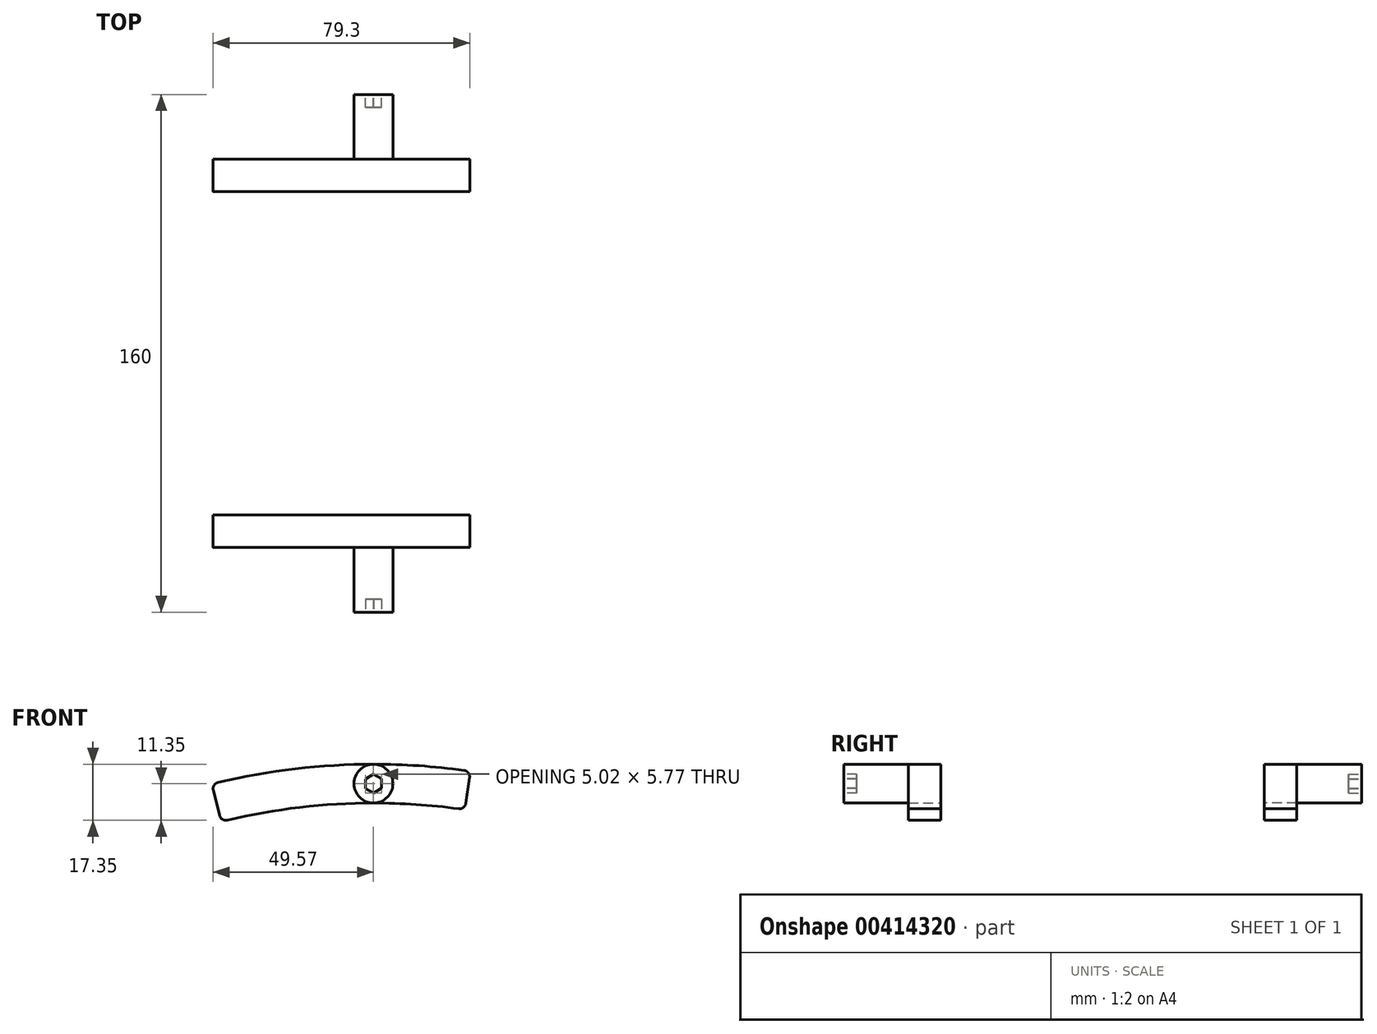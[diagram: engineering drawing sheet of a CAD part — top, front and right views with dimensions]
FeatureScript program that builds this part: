
annotation { "Feature Type Name" : "Feature", "Feature Type Description" : "" }
export const myFeature = defineFeature(function(context is Context, id is Id, definition is map)
    precondition{}
    {
        {
            var Q0;
            Q0=qCreatedBy(makeId("Front.planeOp"),FACE);
            var sketch = newSketch(context, id + "F0", { "sketchPlane" : qUnion([Q0])});
            skLineSegment(sketch, "E0", {"start": v(0, 0) * mm, "end": v(0, 276.46) * mm});
            skCircle(sketch, "E1", {"center": v(0, 0) * mm, "radius": 201.5 * mm, "construction": true});
            skCircle(sketch, "E2", {"center": v(0, 201.5) * mm, "radius": 3 * mm});
            skCircle(sketch, "E3", {"center": v(0, 201.5) * mm, "radius": 6 * mm});
            skArc(sketch, "E4", {"start": v(28, 205.6) * mm, "mid": v(-10.2, 207.25) * mm, "end": v(-48.04, 201.86) * mm});
            skArc(sketch, "E5", {"start": v(26.3, 193.72) * mm, "mid": v(-9.6, 195.26) * mm, "end": v(-45.18, 190.2) * mm});
            skLineSegment(sketch, "E6", {"start": v(28.55, 195.41) * mm, "end": v(29.7, 203.33) * mm});
            skLineSegment(sketch, "E7", {"start": v(-47.59, 191.67) * mm, "end": v(-49.52, 199.44) * mm});
            skPoint(sketch, "E8.visualSharp", {"position": v(30, 205.32) * mm});
            skArc(sketch, "E8.filletArc", {"start": v(29.7, 203.33) * mm, "mid": v(29.33, 204.82) * mm, "end": v(28, 205.6) * mm});
            skPoint(sketch, "E9.visualSharp", {"position": v(28.27, 193.45) * mm});
            skArc(sketch, "E9.filletArc", {"start": v(26.3, 193.72) * mm, "mid": v(27.78, 194.1) * mm, "end": v(28.55, 195.41) * mm});
            skPoint(sketch, "E10.visualSharp", {"position": v(-47.1, 189.74) * mm});
            skArc(sketch, "E10.filletArc", {"start": v(-47.59, 191.67) * mm, "mid": v(-46.69, 190.44) * mm, "end": v(-45.18, 190.2) * mm});
            skPoint(sketch, "E11.visualSharp", {"position": v(-50, 201.39) * mm});
            skArc(sketch, "E11.filletArc", {"start": v(-48.04, 201.86) * mm, "mid": v(-49.28, 200.96) * mm, "end": v(-49.52, 199.44) * mm});
            skSolve(sketch);
        }
        {
            var Q0;
            Q0=makeQuery(id+"F0.imprint","IMPRINT",FACE,{"disambiguationData":[TD([[makeQuery(id+"F0.imprint","IMPRINT",EDGE,{"derivedFrom":sQuery(id+"F0.wireOp",EDGE,"E7")}),-1.0]])]});
            var Q1;
            {var subQ0=sQuery(id+"F0.wireOp",EDGE,"E2");var subQ1=sQuery(id+"F0.wireOp",EDGE,"E0");var subQ2=makeQuery(id+"F0.imprint","INTERSECT",VERTEX,{"disambiguationData":[OD(0.0)],"derivedFrom":[subQ1,subQ0]});Q1=makeQuery(id+"F0.imprint","IMPRINT",FACE,{"disambiguationData":[TD([[makeQuery(id+"F0.imprint","IMPRINT",EDGE,{"disambiguationData":[TD([[subQ2,1.0]])],"derivedFrom":subQ0}),-1.0]])]});}
            var Q2;
            {var subQ0=sQuery(id+"F0.wireOp",EDGE,"E2");var subQ1=sQuery(id+"F0.wireOp",EDGE,"E0");var subQ2=makeQuery(id+"F0.imprint","INTERSECT",VERTEX,{"disambiguationData":[OD(0.0)],"derivedFrom":[subQ1,subQ0]});Q2=makeQuery(id+"F0.imprint","IMPRINT",FACE,{"disambiguationData":[TD([[makeQuery(id+"F0.imprint","IMPRINT",EDGE,{"disambiguationData":[TD([[subQ2,-1.0]])],"derivedFrom":subQ1}),-1.0]])]});}
            var Q3;
            {var subQ0=sQuery(id+"F0.wireOp",EDGE,"E2");var subQ1=sQuery(id+"F0.wireOp",EDGE,"E0");var subQ2=makeQuery(id+"F0.imprint","INTERSECT",VERTEX,{"disambiguationData":[OD(0.0)],"derivedFrom":[subQ1,subQ0]});Q3=makeQuery(id+"F0.imprint","IMPRINT",FACE,{"disambiguationData":[TD([[makeQuery(id+"F0.imprint","IMPRINT",EDGE,{"disambiguationData":[TD([[subQ2,-1.0]])],"derivedFrom":subQ1}),1.0]])]});}
            var Q4;
            {var subQ0=sQuery(id+"F0.wireOp",EDGE,"E2");var subQ1=sQuery(id+"F0.wireOp",EDGE,"E0");var subQ2=makeQuery(id+"F0.imprint","INTERSECT",VERTEX,{"disambiguationData":[OD(0.0)],"derivedFrom":[subQ1,subQ0]});Q4=makeQuery(id+"F0.imprint","IMPRINT",FACE,{"disambiguationData":[TD([[makeQuery(id+"F0.imprint","IMPRINT",EDGE,{"disambiguationData":[TD([[subQ2,-1.0]])],"derivedFrom":subQ0}),-1.0]])]});}
            var Q5;
            Q5=makeQuery(id+"F0.imprint","IMPRINT",FACE,{"disambiguationData":[TD([[makeQuery(id+"F0.imprint","IMPRINT",EDGE,{"derivedFrom":sQuery(id+"F0.wireOp",EDGE,"E6")}),1.0]])]});
            extrude(context, id + "F1", {"entities" : qUnion([Q0, Q1, Q2, Q3, Q4, Q5]), "depth" : 10 * mm});
        }
        {
            var Q0;
            {var subQ0=sQuery(id+"F0.wireOp",EDGE,"E2");var subQ1=sQuery(id+"F0.wireOp",EDGE,"E0");var subQ2=makeQuery(id+"F0.imprint","INTERSECT",VERTEX,{"disambiguationData":[OD(0.0)],"derivedFrom":[subQ1,subQ0]});Q0=makeQuery(id+"F0.imprint","IMPRINT",FACE,{"disambiguationData":[TD([[makeQuery(id+"F0.imprint","IMPRINT",EDGE,{"disambiguationData":[TD([[subQ2,-1.0]])],"derivedFrom":subQ1}),1.0]])]});}
            var Q1;
            {var subQ0=sQuery(id+"F0.wireOp",EDGE,"E2");var subQ1=sQuery(id+"F0.wireOp",EDGE,"E0");var subQ2=makeQuery(id+"F0.imprint","INTERSECT",VERTEX,{"disambiguationData":[OD(0.0)],"derivedFrom":[subQ1,subQ0]});Q1=makeQuery(id+"F0.imprint","IMPRINT",FACE,{"disambiguationData":[TD([[makeQuery(id+"F0.imprint","IMPRINT",EDGE,{"disambiguationData":[TD([[subQ2,-1.0]])],"derivedFrom":subQ1}),-1.0]])]});}
            var Q2;
            {var subQ0=sQuery(id+"F0.wireOp",EDGE,"E2");var subQ1=sQuery(id+"F0.wireOp",EDGE,"E0");var subQ2=makeQuery(id+"F0.imprint","INTERSECT",VERTEX,{"disambiguationData":[OD(0.0)],"derivedFrom":[subQ1,subQ0]});Q2=makeQuery(id+"F0.imprint","IMPRINT",FACE,{"disambiguationData":[TD([[makeQuery(id+"F0.imprint","IMPRINT",EDGE,{"disambiguationData":[TD([[subQ2,1.0]])],"derivedFrom":subQ0}),-1.0]])]});}
            var Q3;
            {var subQ0=sQuery(id+"F0.wireOp",EDGE,"E2");var subQ1=sQuery(id+"F0.wireOp",EDGE,"E0");var subQ2=makeQuery(id+"F0.imprint","INTERSECT",VERTEX,{"disambiguationData":[OD(0.0)],"derivedFrom":[subQ1,subQ0]});Q3=makeQuery(id+"F0.imprint","IMPRINT",FACE,{"disambiguationData":[TD([[makeQuery(id+"F0.imprint","IMPRINT",EDGE,{"disambiguationData":[TD([[subQ2,-1.0]])],"derivedFrom":subQ0}),-1.0]])]});}
            extrude(context, id + "F2", {"entities" : qUnion([Q0, Q1, Q2, Q3]), "operationType" : NewBodyOperationType.ADD, "depth" : 30 * mm});
        }
        {
            var Q0;
            Q0=makeQuery(id+"F2.opExtrude","CAP_FACE",FACE,{"disambiguationData":[OSD([sQuery(id+"F0.wireOp",EDGE,"E3")])],"isStart":false});
            var sketch = newSketch(context, id + "F3", { "sketchPlane" : qUnion([Q0])});
            skCircle(sketch, "E12.cCircle", {"center": v(0, 201.5) * mm, "radius": 2.5 * mm, "construction": true});
            skLineSegment(sketch, "E12.0", {"start": v(2.51, 200.08) * mm, "end": v(0.02, 198.61) * mm});
            skLineSegment(sketch, "E12.1", {"start": v(0.02, 198.61) * mm, "end": v(-2.49, 200.04) * mm});
            skLineSegment(sketch, "E12.2", {"start": v(-2.49, 200.04) * mm, "end": v(-2.51, 202.92) * mm});
            skLineSegment(sketch, "E12.3", {"start": v(-2.51, 202.92) * mm, "end": v(-0.02, 204.39) * mm});
            skLineSegment(sketch, "E12.4", {"start": v(-0.02, 204.39) * mm, "end": v(2.49, 202.96) * mm});
            skLineSegment(sketch, "E12.5", {"start": v(2.49, 202.96) * mm, "end": v(2.51, 200.08) * mm});
            skPoint(sketch, "E12.0.midPoint", {"position": v(1.27, 199.34) * mm});
            skSolve(sketch);
        }
        {
            var Q0;
            Q0=makeQuery(id+"F3.imprint","IMPRINT",FACE,{"disambiguationData":[TD([[makeQuery(id+"F3.imprint","IMPRINT",EDGE,{"derivedFrom":sQuery(id+"F3.wireOp",EDGE,"E12.0")}),-1.0]])]});
            extrude(context, id + "F4", {"entities" : qUnion([Q0]), "operationType" : NewBodyOperationType.REMOVE, "oppositeDirection" : true, "depth" : 4 * mm});
        }
        {
            var Q0;
            Q0=qCreatedBy(makeId("Front.planeOp"),FACE);
            cPlane(context, id + "F5", {"entities" : qUnion([Q0]), "cplaneType" : CPlaneType.OFFSET, "offset" : 50 * mm, "oppositeDirection" : true, "width" : 150 * mm, "height" : 150 * mm});
        }
        {
            var Q0;
            Q0=makeQuery(id+"F1.opExtrude","SWEPT_BODY",BODY,{"disambiguationData":[OSD([sQuery(id+"F0.wireOp",EDGE,"E4"),sQuery(id+"F0.wireOp",EDGE,"E5"),sQuery(id+"F0.wireOp",EDGE,"E6"),sQuery(id+"F0.wireOp",EDGE,"E7"),sQuery(id+"F0.wireOp",EDGE,"E8.filletArc"),sQuery(id+"F0.wireOp",EDGE,"E9.filletArc"),sQuery(id+"F0.wireOp",EDGE,"E10.filletArc"),sQuery(id+"F0.wireOp",EDGE,"E11.filletArc")])]});
            var Q1;
            Q1=qCreatedBy(id+"F5.planeOp",FACE);
            mirror(context, id + "F6", {"entities" : qUnion([Q0]), "mirrorPlane" : qUnion([Q1])});
        }
    });
